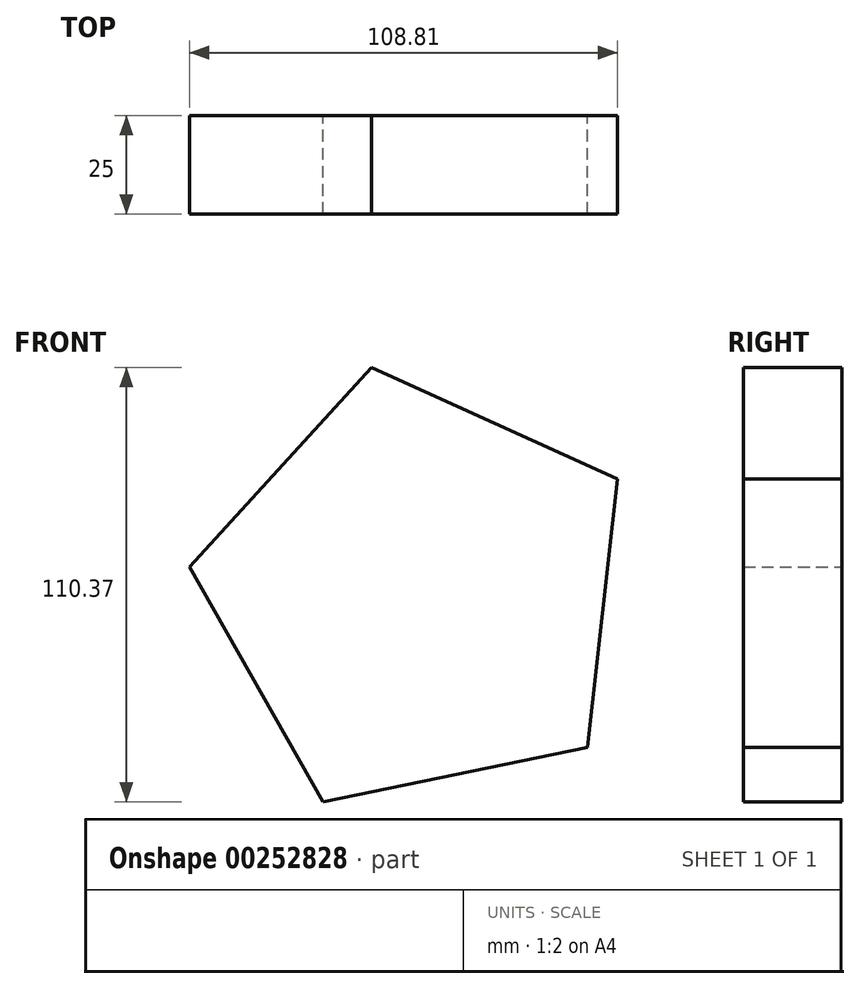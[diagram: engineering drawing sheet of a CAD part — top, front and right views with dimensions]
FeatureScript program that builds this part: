
annotation { "Feature Type Name" : "Feature", "Feature Type Description" : "" }
export const myFeature = defineFeature(function(context is Context, id is Id, definition is map)
    precondition{}
    {
        {
            var Q0;
            Q0=qCreatedBy(makeId("Front.planeOp"),FACE);
            var sketch = newSketch(context, id + "F0", { "sketchPlane" : qUnion([Q0])});
            skCircle(sketch, "E0.cCircle", {"center": v(0, 0) * mm, "radius": 58.4 * mm, "construction": true});
            skLineSegment(sketch, "E0.0", {"start": v(50.78, 28.83) * mm, "end": v(43.11, -39.38) * mm});
            skLineSegment(sketch, "E0.1", {"start": v(43.11, -39.38) * mm, "end": v(-24.13, -53.17) * mm});
            skLineSegment(sketch, "E0.2", {"start": v(-24.13, -53.17) * mm, "end": v(-58.03, 6.52) * mm});
            skLineSegment(sketch, "E0.3", {"start": v(-58.03, 6.52) * mm, "end": v(-11.73, 57.2) * mm});
            skLineSegment(sketch, "E0.4", {"start": v(-11.73, 57.2) * mm, "end": v(50.78, 28.83) * mm});
            skSolve(sketch);
        }
        {
            var Q0;
            Q0 = qSketchRegion(id + "F0", true);
            extrude(context, id + "F1", {"entities" : qUnion([Q0]), "depth" : 25 * mm});
        }
    });
